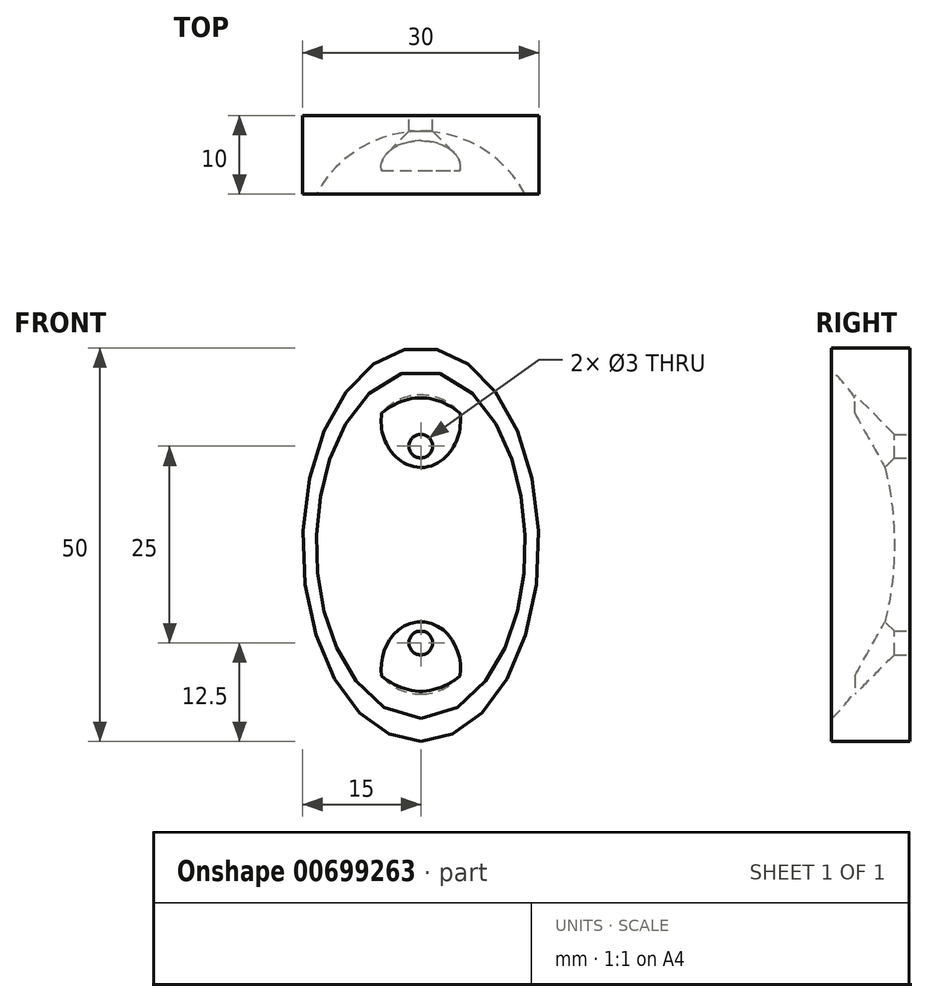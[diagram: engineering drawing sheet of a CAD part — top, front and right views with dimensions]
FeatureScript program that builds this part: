
annotation { "Feature Type Name" : "Feature", "Feature Type Description" : "" }
export const myFeature = defineFeature(function(context is Context, id is Id, definition is map)
    precondition{}
    {
        {
            var Q0;
            Q0=qCreatedBy(makeId("Front.planeOp"),FACE);
            var sketch = newSketch(context, id + "F0", { "sketchPlane" : qUnion([Q0])});
            skEllipse(sketch, "E0", {"center": v(0, 0) * mm, "majorRadius": 25 * mm, "minorRadius": 15 * mm, "majorAxis": v(0, -1)});
            skSolve(sketch);
        }
        {
            var Q0;
            Q0 = qSketchRegion(id + "F0", true);
            extrude(context, id + "F1", {"entities" : qUnion([Q0]), "depth" : 10 * mm, "offsetDistance" : 25 * mm});
        }
        {
            var Q0;
            Q0=qCreatedBy(makeId("Right.planeOp"),FACE);
            var sketch = newSketch(context, id + "F2", { "sketchPlane" : qUnion([Q0])});
            skEllipse(sketch, "E1", {"center": v(-17, 0) * mm, "majorRadius": 25 * mm, "minorRadius": 15 * mm, "majorAxis": v(0, -1)});
            skLineSegment(sketch, "E2", {"start": v(-17, 49.43) * mm, "end": v(-17, -57.65) * mm});
            skSolve(sketch);
        }
        {
            var Q0;
            {var subQ0=sQuery(id+"F2.wireOp",EDGE,"E2");var subQ1=sQuery(id+"F2.wireOp",EDGE,"E1");var subQ2=makeQuery(id+"F2.imprint","INTERSECT",VERTEX,{"disambiguationData":[OD(0.0)],"derivedFrom":[subQ1,subQ0]});Q0=makeQuery(id+"F2.imprint","IMPRINT",FACE,{"disambiguationData":[TD([[makeQuery(id+"F2.imprint","IMPRINT",EDGE,{"disambiguationData":[TD([[subQ2,-1.0]])],"derivedFrom":subQ1}),1.0]])]});}
            var Q1;
            Q1=sQuery(id+"F2.wireOp",EDGE,"E2");
            revolve(context, id + "F3", {"operationType" : NewBodyOperationType.REMOVE, "surfaceOperationType" : NewSurfaceOperationType.NEW, "entities" : qUnion([Q0]), "axis" : qUnion([Q1]), "revolveType" : RevolveType.TWO_DIRECTIONS, "oppositeDirection" : true, "angle" : 90 * degree, "angleBack" : 90 * degree});
        }
        {
            var Q0;
            Q0=qCreatedBy(makeId("Front.planeOp"),FACE);
            var sketch = newSketch(context, id + "F4", { "sketchPlane" : qUnion([Q0])});
            skCircle(sketch, "E3", {"center": v(0, 12.5) * mm, "radius": 1.5 * mm});
            skCircle(sketch, "E4", {"center": v(0, -12.5) * mm, "radius": 1.5 * mm});
            skSolve(sketch);
        }
        {
            var Q0;
            Q0=makeQuery(id+"F4.imprint","IMPRINT",FACE,{"disambiguationData":[TD([[makeQuery(id+"F4.imprint","IMPRINT",EDGE,{"derivedFrom":sQuery(id+"F4.wireOp",EDGE,"E4")}),1.0]])]});
            var Q1;
            Q1=makeQuery(id+"F4.imprint","IMPRINT",FACE,{"disambiguationData":[TD([[makeQuery(id+"F4.imprint","IMPRINT",EDGE,{"derivedFrom":sQuery(id+"F4.wireOp",EDGE,"E3")}),1.0]])]});
            extrude(context, id + "F5", {"entities" : qUnion([Q0, Q1]), "operationType" : NewBodyOperationType.REMOVE, "depth" : 2 * mm, "offsetDistance" : 25 * mm});
        }
        {
            var Q0;
            Q0=makeQuery(id+"F5.boolean.opBoolean","COPY",FACE,{"derivedFrom":makeQuery(id+"F5.opExtrude","CAP_FACE",FACE,{"disambiguationData":[OSD([sQuery(id+"F4.wireOp",EDGE,"E4")])],"isStart":false})});
            var Q1;
            Q1=makeQuery(id+"F5.boolean.opBoolean","COPY",FACE,{"derivedFrom":makeQuery(id+"F5.opExtrude","CAP_FACE",FACE,{"disambiguationData":[OSD([sQuery(id+"F4.wireOp",EDGE,"E3")])],"isStart":false})});
            extrude(context, id + "F6", {"entities" : qUnion([Q0, Q1]), "operationType" : NewBodyOperationType.REMOVE, "oppositeDirection" : true, "depth" : 5 * mm, "offsetDistance" : 25 * mm, "hasDraft" : true, "draftAngle" : 45 * degree});
        }
    });
